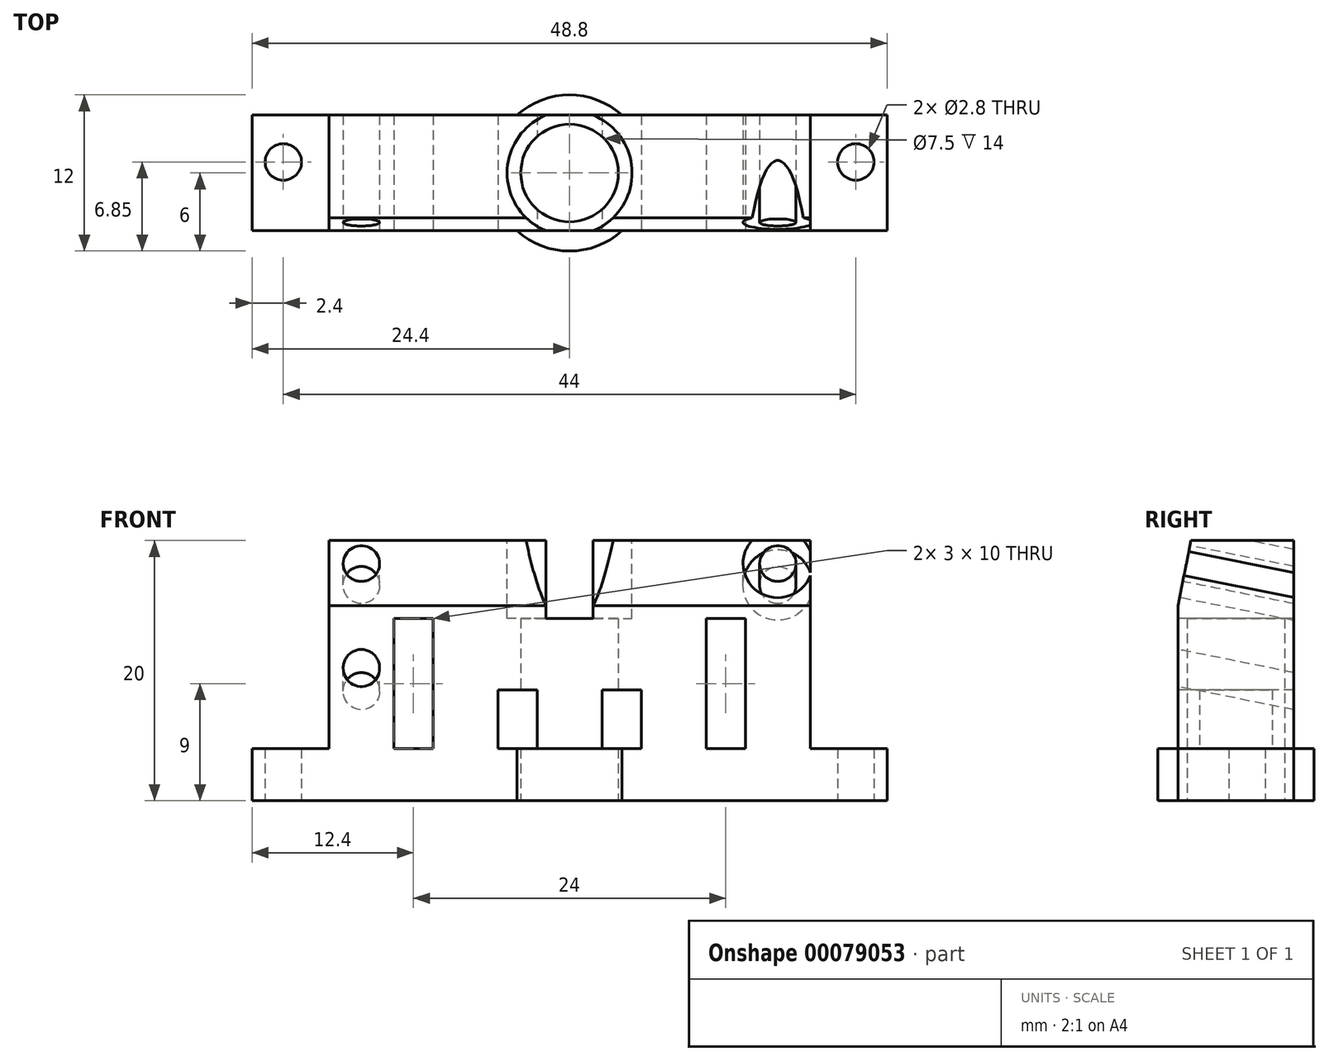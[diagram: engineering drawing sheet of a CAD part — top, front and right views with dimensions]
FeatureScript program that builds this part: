
annotation { "Feature Type Name" : "Feature", "Feature Type Description" : "" }
export const myFeature = defineFeature(function(context is Context, id is Id, definition is map)
    precondition{}
    {
        {
            var Q0;
            Q0=qCreatedBy(makeId("Top.planeOp"),FACE);
            var sketch = newSketch(context, id + "F0", { "sketchPlane" : qUnion([Q0])});
            skCircle(sketch, "E0", {"center": v(-22, 0) * mm, "radius": 1.4 * mm});
            skLineSegment(sketch, "E1", {"start": v(0, 19.31) * mm, "end": v(0, -21.5) * mm, "construction": true});
            skCircle(sketch, "E2.MirrorC", {"center": v(22, 0) * mm, "radius": 1.4 * mm});
            skCircle(sketch, "E3", {"center": v(0, -0.85) * mm, "radius": 3.25 * mm, "construction": true});
            skLineSegment(sketch, "E4", {"start": v(-26.06, 2.4) * mm, "end": v(29.67, 2.4) * mm, "construction": true});
            skLineSegment(sketch, "E5.bottom", {"start": v(-24.4, 3.6) * mm, "end": v(24.4, 3.6) * mm});
            skLineSegment(sketch, "E5.top", {"start": v(-24.4, -5.3) * mm, "end": v(24.4, -5.3) * mm});
            skLineSegment(sketch, "E5.left", {"start": v(-24.4, 3.6) * mm, "end": v(-24.4, -5.3) * mm});
            skLineSegment(sketch, "E5.right", {"start": v(24.4, 3.6) * mm, "end": v(24.4, -5.3) * mm});
            skCircle(sketch, "E6.0", {"center": v(0, -0.85) * mm, "radius": 3.75 * mm});
            skArc(sketch, "E7", {"start": v(-4.03, -5.3) * mm, "mid": v(0, -6.85) * mm, "end": v(4.03, -5.3) * mm});
            skArc(sketch, "E8.trimOffspring", {"start": v(4.03, 3.6) * mm, "mid": v(0, 5.15) * mm, "end": v(-4.03, 3.6) * mm});
            skSolve(sketch);
        }
        {
            var Q0;
            Q0=makeQuery(id+"F0.imprint","IMPRINT",FACE,{"disambiguationData":[TD([[makeQuery(id+"F0.imprint","IMPRINT",EDGE,{"derivedFrom":sQuery(id+"F0.wireOp",EDGE,"E0")}),-1.0]])]});
            extrude(context, id + "F1", {"entities" : qUnion([Q0]), "depth" : 20 * mm});
        }
        {
            var Q0;
            Q0=makeQuery(id+"F1.opExtrude","CAP_FACE",FACE,{"disambiguationData":[OSD([sQuery(id+"F0.wireOp",EDGE,"E0"),sQuery(id+"F0.wireOp",EDGE,"E2.MirrorC"),sQuery(id+"F0.wireOp",EDGE,"E3"),sQuery(id+"F0.wireOp",EDGE,"E5.bottom"),sQuery(id+"F0.wireOp",EDGE,"E5.top"),sQuery(id+"F0.wireOp",EDGE,"E5.left"),sQuery(id+"F0.wireOp",EDGE,"E5.right")])],"isStart":false});
            var sketch = newSketch(context, id + "F2", { "sketchPlane" : qUnion([Q0])});
            skCircle(sketch, "E9", {"center": v(0, -0.85) * mm, "radius": 4.8 * mm});
            skCircle(sketch, "E10.0", {"center": v(0, -0.85) * mm, "radius": 6.8 * mm});
            skSolve(sketch);
        }
        {
            var Q0;
            Q0=makeQuery(id+"F2.imprint","IMPRINT",FACE,{"disambiguationData":[TD([[makeQuery(id+"F2.imprint","IMPRINT",EDGE,{"derivedFrom":sQuery(id+"F2.wireOp",EDGE,"E9")}),1.0]])]});
            var Q1;
            {var subQ0=sQuery(id+"F2.wireOp",EDGE,"E9");var subQ1=makeQuery(id+"F1.opExtrude","CAP_EDGE",EDGE,{"disambiguationData":[OSD([sQuery(id+"F0.wireOp",EDGE,"E5.bottom")])],"isStart":false});var subQ2=makeQuery(id+"F2.imprint","INTERSECT",VERTEX,{"disambiguationData":[OD(0.0)],"derivedFrom":[subQ1,subQ0]});Q1=makeQuery(id+"F2.imprint","IMPRINT",FACE,{"disambiguationData":[TD([[makeQuery(id+"F2.imprint","IMPRINT",EDGE,{"disambiguationData":[TD([[subQ2,1.0]])],"derivedFrom":subQ0}),1.0]])]});}
            var Q2;
            {var subQ0=sQuery(id+"F2.wireOp",EDGE,"E9");var subQ1=makeQuery(id+"F1.opExtrude","CAP_EDGE",EDGE,{"disambiguationData":[OSD([sQuery(id+"F0.wireOp",EDGE,"E5.top")])],"isStart":false});var subQ2=makeQuery(id+"F2.imprint","INTERSECT",VERTEX,{"disambiguationData":[OD(0.0)],"derivedFrom":[subQ1,subQ0]});Q2=makeQuery(id+"F2.imprint","IMPRINT",FACE,{"disambiguationData":[TD([[makeQuery(id+"F2.imprint","IMPRINT",EDGE,{"disambiguationData":[TD([[subQ2,-1.0]])],"derivedFrom":subQ0}),1.0]])]});}
            extrude(context, id + "F3", {"entities" : qUnion([Q0, Q1, Q2]), "operationType" : NewBodyOperationType.REMOVE, "oppositeDirection" : true, "depth" : 6 * mm});
        }
        {
            var Q0;
            {var subQ2=sQuery(id+"F0.wireOp",EDGE,"E5.top");var subQ3=sQuery(id+"F0.wireOp",EDGE,"E5.right");var subQ4=makeQuery(id+"F1.opExtrude","CAP_EDGE",EDGE,{"disambiguationData":[OSD([subQ2])],"isStart":false});Q0=makeQuery(id+"FnIOA2Ro6AQeCIU_1.boolean.opBoolean","SPLIT",EDGE,{"disambiguationData":[TD([makeQuery(id+"F1.opExtrude","SWEPT_FACE",FACE,{"disambiguationData":[OSD([subQ3])]})])],"derivedFrom":subQ4});}
            var Q1;
            {var subQ2=sQuery(id+"F0.wireOp",EDGE,"E5.left");var subQ3=sQuery(id+"F0.wireOp",EDGE,"E5.top");var subQ4=makeQuery(id+"F1.opExtrude","CAP_EDGE",EDGE,{"disambiguationData":[OSD([subQ3])],"isStart":false});Q1=makeQuery(id+"FnIOA2Ro6AQeCIU_1.boolean.opBoolean","SPLIT",EDGE,{"disambiguationData":[TD([makeQuery(id+"F1.opExtrude","SWEPT_FACE",FACE,{"disambiguationData":[OSD([subQ2])]})])],"derivedFrom":subQ4});}
            chamfer(context, id + "F4", {"entities" : qUnion([Q0, Q1]), "chamferType" : ChamferType.TWO_OFFSETS, "width1" : 1 * mm, "oppositeDirection" : false, "width2" : 5 * mm, "tangentPropagation" : true});
        }
        {
            var Q0;
            {var subQ2=sQuery(id+"F0.wireOp",EDGE,"E5.left");var subQ3=sQuery(id+"F0.wireOp",EDGE,"E5.top");var subQ4=makeQuery(id+"F1.opExtrude","CAP_EDGE",EDGE,{"disambiguationData":[OSD([subQ3])],"isStart":false});Q0=makeQuery(id+"F4.opChamfer","BLEND_FACE",FACE,{"disambiguationData":[OSD([subQ3]),TDD([makeQuery(id+"FnIOA2Ro6AQeCIU_1.boolean.opBoolean","SPLIT",EDGE,{"disambiguationData":[TD([makeQuery(id+"F1.opExtrude","SWEPT_FACE",FACE,{"disambiguationData":[OSD([subQ2])]})])],"derivedFrom":subQ4})])]});}
            var sketch = newSketch(context, id + "F5", { "sketchPlane" : qUnion([Q0])});
            skLineSegment(sketch, "E11.0", {"start": v(-24.4, -1.04) * mm, "end": v(24.4, -1.04) * mm});
            skCircle(sketch, "E12", {"center": v(-16, 16.96) * mm, "radius": 1.4 * mm});
            skLineSegment(sketch, "E13", {"start": v(0, -1.04) * mm, "end": v(0, 30) * mm, "construction": true});
            skPoint(sketch, "E13.endSnap0", {"position": v(0, -1.04) * mm});
            skCircle(sketch, "E14.MirrorC", {"center": v(16, 16.96) * mm, "radius": 1.4 * mm});
            skCircle(sketch, "E15", {"center": v(-16, 16.96) * mm, "radius": 2.67 * mm});
            skCircle(sketch, "E16.MirrorC", {"center": v(16, 16.96) * mm, "radius": 2.67 * mm});
            skCircle(sketch, "E17.0.1.0", {"center": v(-16, 8.96) * mm, "radius": 1.4 * mm});
            skCircle(sketch, "E17.0.1.1", {"center": v(16, 8.96) * mm, "radius": 1.4 * mm});
            skLineSegment(sketch, "E17.direction1", {"start": v(-16, 16.96) * mm, "end": v(9, 16.96) * mm, "construction": true});
            skLineSegment(sketch, "E17.direction2", {"start": v(-16, 16.96) * mm, "end": v(-16, 8.96) * mm, "construction": true});
            skSolve(sketch);
        }
        {
            var Q0;
            Q0=makeQuery(id+"F5.imprint","IMPRINT",FACE,{"disambiguationData":[TD([[makeQuery(id+"F5.imprint","IMPRINT",EDGE,{"derivedFrom":sQuery(id+"F5.wireOp",EDGE,"E12")}),1.0]])]});
            var Q1;
            Q1=makeQuery(id+"F5.imprint","IMPRINT",FACE,{"disambiguationData":[TD([[makeQuery(id+"F5.imprint","IMPRINT",EDGE,{"derivedFrom":sQuery(id+"F5.wireOp",EDGE,"E14.MirrorC")}),-1.0]])]});
            var Q2;
            Q2=makeQuery(id+"F5.imprint","IMPRINT",FACE,{"disambiguationData":[TD([[makeQuery(id+"F5.imprint","IMPRINT",EDGE,{"derivedFrom":sQuery(id+"F5.wireOp",EDGE,"E17.0.1.0")}),1.0]])]});
            var Q3;
            Q3=makeQuery(id+"F5.imprint","IMPRINT",FACE,{"disambiguationData":[TD([[makeQuery(id+"F5.imprint","IMPRINT",EDGE,{"derivedFrom":sQuery(id+"F5.wireOp",EDGE,"E17.0.1.1")}),-1.0]])]});
            extrude(context, id + "F6", {"entities" : qUnion([Q0, Q1, Q2, Q3]), "operationType" : NewBodyOperationType.REMOVE, "oppositeDirection" : true, "depth" : 25 * mm});
        }
        {
            var Q0;
            Q0=makeQuery(id+"F1.opExtrude","SWEPT_FACE",FACE,{"disambiguationData":[OSD([sQuery(id+"F0.wireOp",EDGE,"E5.top")])]});
            var sketch = newSketch(context, id + "F7", { "sketchPlane" : qUnion([Q0])});
            skLineSegment(sketch, "E18.bottom", {"start": v(-21.5, 14) * mm, "end": v(-18.5, 14) * mm});
            skLineSegment(sketch, "E18.top", {"start": v(-21.5, 4) * mm, "end": v(-18.5, 4) * mm});
            skLineSegment(sketch, "E18.left", {"start": v(-21.5, 14) * mm, "end": v(-21.5, 4) * mm});
            skLineSegment(sketch, "E18.right", {"start": v(-18.5, 14) * mm, "end": v(-18.5, 4) * mm});
            skLineSegment(sketch, "E19.1.0.0", {"start": v(-10.5, 14) * mm, "end": v(-10.5, 4) * mm});
            skLineSegment(sketch, "E19.1.0.1", {"start": v(-13.5, 14) * mm, "end": v(-10.5, 14) * mm});
            skLineSegment(sketch, "E19.1.0.2", {"start": v(-13.5, 14) * mm, "end": v(-13.5, 4) * mm});
            skLineSegment(sketch, "E19.1.0.3", {"start": v(-13.5, 4) * mm, "end": v(-10.5, 4) * mm});
            skLineSegment(sketch, "E19.2.0.0", {"start": v(-2.5, 14) * mm, "end": v(-2.5, 4) * mm});
            skLineSegment(sketch, "E19.2.0.1", {"start": v(-5.5, 14) * mm, "end": v(-2.5, 14) * mm});
            skLineSegment(sketch, "E19.2.0.2", {"start": v(-5.5, 14) * mm, "end": v(-5.5, 4) * mm});
            skLineSegment(sketch, "E19.2.0.3", {"start": v(-5.5, 4) * mm, "end": v(-2.5, 4) * mm});
            skLineSegment(sketch, "E19.3.0.0", {"start": v(5.5, 14) * mm, "end": v(5.5, 4) * mm});
            skLineSegment(sketch, "E19.3.0.1", {"start": v(2.5, 14) * mm, "end": v(5.5, 14) * mm});
            skLineSegment(sketch, "E19.3.0.2", {"start": v(2.5, 14) * mm, "end": v(2.5, 4) * mm});
            skLineSegment(sketch, "E19.3.0.3", {"start": v(2.5, 4) * mm, "end": v(5.5, 4) * mm});
            skLineSegment(sketch, "E19.4.0.0", {"start": v(13.5, 14) * mm, "end": v(13.5, 4) * mm});
            skLineSegment(sketch, "E19.4.0.1", {"start": v(10.5, 14) * mm, "end": v(13.5, 14) * mm});
            skLineSegment(sketch, "E19.4.0.2", {"start": v(10.5, 14) * mm, "end": v(10.5, 4) * mm});
            skLineSegment(sketch, "E19.4.0.3", {"start": v(10.5, 4) * mm, "end": v(13.5, 4) * mm});
            skLineSegment(sketch, "E19.5.0.0", {"start": v(21.5, 14) * mm, "end": v(21.5, 4) * mm});
            skLineSegment(sketch, "E19.5.0.1", {"start": v(18.5, 14) * mm, "end": v(21.5, 14) * mm});
            skLineSegment(sketch, "E19.5.0.2", {"start": v(18.5, 14) * mm, "end": v(18.5, 4) * mm});
            skLineSegment(sketch, "E19.5.0.3", {"start": v(18.5, 4) * mm, "end": v(21.5, 4) * mm});
            skLineSegment(sketch, "E19.direction1", {"start": v(-18.5, 4) * mm, "end": v(-10.5, 4) * mm, "construction": true});
            skLineSegment(sketch, "E20", {"start": v(-5.5, 8.5) * mm, "end": v(5.5, 8.5) * mm});
            skPoint(sketch, "E21.0", {"position": v(0, 0) * mm});
            skLineSegment(sketch, "E22", {"start": v(0, 0) * mm, "end": v(0, 8.5) * mm, "construction": true});
            skLineSegment(sketch, "E23.0", {"start": v(-24.4, 20) * mm, "end": v(-5.62, 20) * mm});
            skLineSegment(sketch, "E24.0", {"start": v(-24.4, 15) * mm, "end": v(-24.4, 20) * mm});
            skLineSegment(sketch, "E25.0", {"start": v(24.4, 20) * mm, "end": v(24.4, 15) * mm});
            skLineSegment(sketch, "E26.0", {"start": v(-24.4, 15) * mm, "end": v(-24.4, 0) * mm});
            skLineSegment(sketch, "E27.0", {"start": v(-24.4, 0) * mm, "end": v(24.4, 0) * mm});
            skLineSegment(sketch, "E28.0", {"start": v(24.4, 15) * mm, "end": v(24.4, 0) * mm});
            skLineSegment(sketch, "E29", {"start": v(-21.5, 4) * mm, "end": v(-24.4, 4) * mm});
            skLineSegment(sketch, "E30", {"start": v(21.5, 4) * mm, "end": v(24.4, 4) * mm});
            skLineSegment(sketch, "E31", {"start": v(-18.5, 14) * mm, "end": v(-18.5, 20) * mm});
            skLineSegment(sketch, "E32", {"start": v(18.5, 14) * mm, "end": v(18.5, 20) * mm});
            skLineSegment(sketch, "E33.0", {"start": v(3.34, 20) * mm, "end": v(24.4, 20) * mm});
            skSolve(sketch);
        }
        {
            var Q0;
            Q0=makeQuery(id+"F7.imprint","IMPRINT",FACE,{"disambiguationData":[TD([[makeQuery(id+"F7.imprint","IMPRINT",EDGE,{"derivedFrom":sQuery(id+"F7.wireOp",EDGE,"E18.bottom")}),-1.0]])]});
            var Q1;
            {var subQ0=sQuery(id+"F7.wireOp",EDGE,"E19.2.0.3");Q1=makeQuery(id+"F7.imprint","IMPRINT",FACE,{"disambiguationData":[TD([[makeQuery(id+"F7.imprint","IMPRINT",EDGE,{"derivedFrom":subQ0}),1.0]])]});}
            var Q2;
            {var subQ0=sQuery(id+"F7.wireOp",EDGE,"E19.3.0.3");Q2=makeQuery(id+"F7.imprint","IMPRINT",FACE,{"disambiguationData":[TD([[makeQuery(id+"F7.imprint","IMPRINT",EDGE,{"derivedFrom":subQ0}),1.0]])]});}
            var Q3;
            Q3=makeQuery(id+"F7.imprint","IMPRINT",FACE,{"disambiguationData":[TD([[makeQuery(id+"F7.imprint","IMPRINT",EDGE,{"derivedFrom":sQuery(id+"F7.wireOp",EDGE,"E19.4.0.0")}),-1.0]])]});
            var Q4;
            Q4=makeQuery(id+"F7.imprint","IMPRINT",FACE,{"disambiguationData":[TD([[makeQuery(id+"F7.imprint","IMPRINT",EDGE,{"derivedFrom":sQuery(id+"F7.wireOp",EDGE,"E19.5.0.0")}),-1.0]])]});
            var Q5;
            {var subQ10=sQuery(id+"F7.wireOp",EDGE,"E18.left");Q5=makeQuery(id+"F7.imprint","IMPRINT",FACE,{"disambiguationData":[TD([[makeQuery(id+"F7.imprint","IMPRINT",EDGE,{"derivedFrom":subQ10}),-1.0]])]});}
            var Q6;
            {var subQ11=sQuery(id+"F7.wireOp",EDGE,"E24.0");Q6=makeQuery(id+"F7.imprint","IMPRINT",FACE,{"disambiguationData":[TD([[makeQuery(id+"F7.imprint","IMPRINT",EDGE,{"derivedFrom":subQ11}),-1.0]])]});}
            var Q7;
            {var subQ11=sQuery(id+"F7.wireOp",EDGE,"E25.0");Q7=makeQuery(id+"F7.imprint","IMPRINT",FACE,{"disambiguationData":[TD([[makeQuery(id+"F7.imprint","IMPRINT",EDGE,{"derivedFrom":subQ11}),-1.0]])]});}
            var Q8;
            {var subQ11=sQuery(id+"F7.wireOp",EDGE,"E19.5.0.0");Q8=makeQuery(id+"F7.imprint","IMPRINT",FACE,{"disambiguationData":[TD([[makeQuery(id+"F7.imprint","IMPRINT",EDGE,{"derivedFrom":subQ11}),1.0]])]});}
            var Q9;
            Q9=makeQuery(id+"F7.imprint","IMPRINT",FACE,{"disambiguationData":[TD([[makeQuery(id+"F7.imprint","IMPRINT",EDGE,{"derivedFrom":sQuery(id+"F7.wireOp",EDGE,"E19.1.0.0")}),-1.0]])]});
            extrude(context, id + "F8", {"entities" : qUnion([Q0, Q1, Q2, Q3, Q4, Q5, Q6, Q7, Q8, Q9]), "operationType" : NewBodyOperationType.REMOVE, "oppositeDirection" : true, "depth" : 25 * mm});
        }
        {
            var Q0;
            {var subQ0=sQuery(id+"F0.wireOp",EDGE,"E7");Q0=makeQuery(id+"F0.imprint","IMPRINT",FACE,{"disambiguationData":[TD([[makeQuery(id+"F0.imprint","IMPRINT",EDGE,{"derivedFrom":subQ0}),1.0]])]});}
            var Q1;
            {var subQ0=sQuery(id+"F0.wireOp",EDGE,"E8.trimOffspring");Q1=makeQuery(id+"F0.imprint","IMPRINT",FACE,{"disambiguationData":[TD([[makeQuery(id+"F0.imprint","IMPRINT",EDGE,{"derivedFrom":subQ0}),1.0]])]});}
            extrude(context, id + "F9", {"entities" : qUnion([Q0, Q1]), "operationType" : NewBodyOperationType.ADD, "depth" : 4 * mm});
        }
    });
